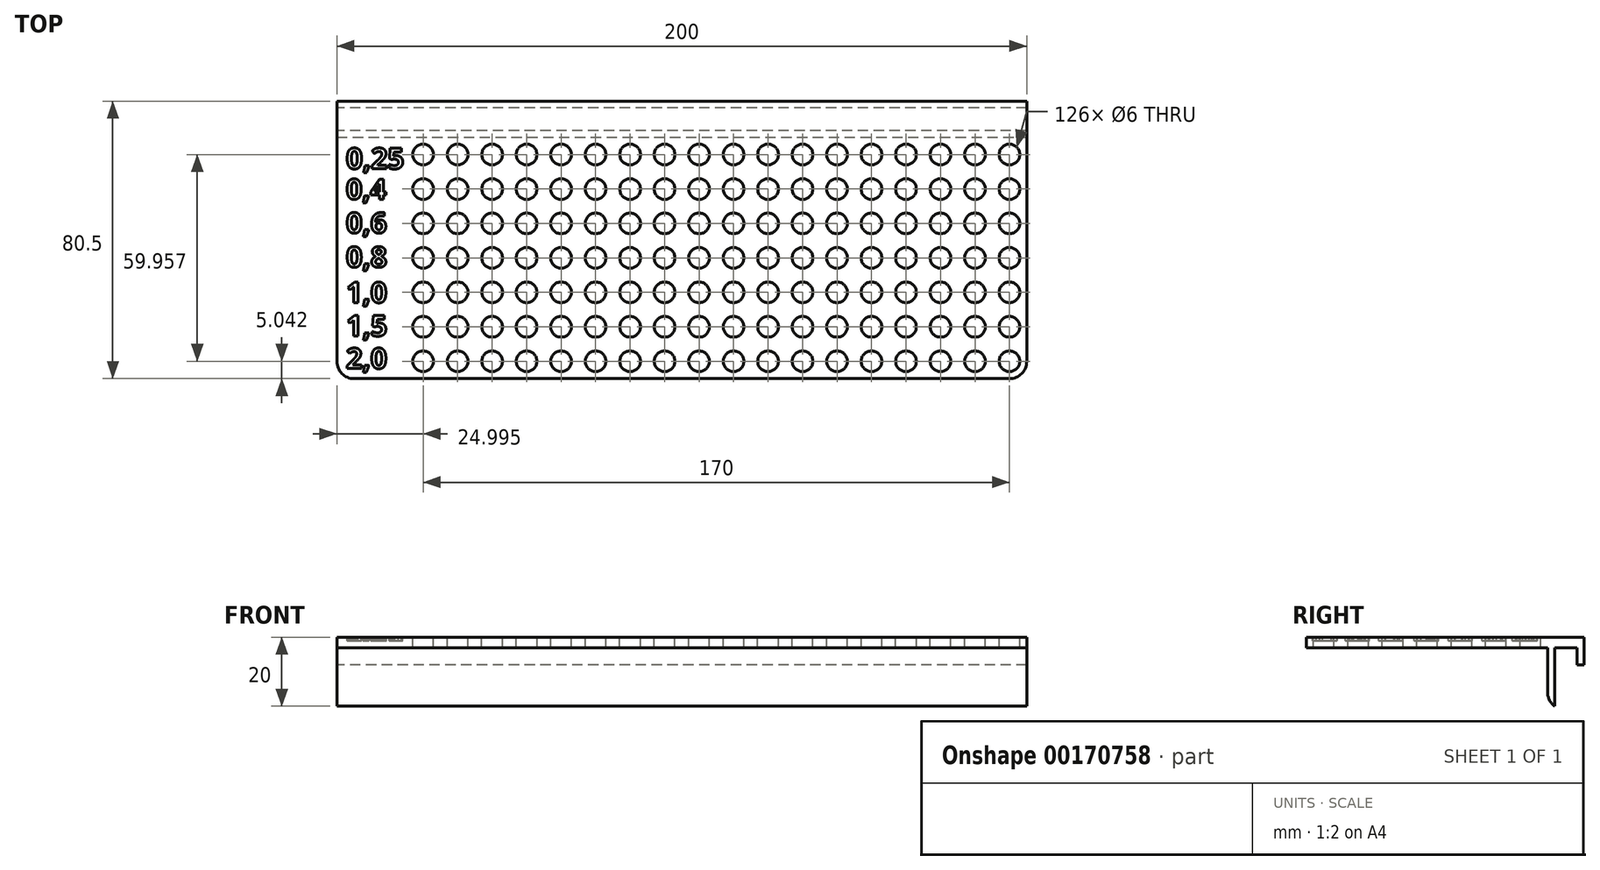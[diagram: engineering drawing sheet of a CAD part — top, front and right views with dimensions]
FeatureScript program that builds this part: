
annotation { "Feature Type Name" : "Feature", "Feature Type Description" : "" }
export const myFeature = defineFeature(function(context is Context, id is Id, definition is map)
    precondition{}
    {
        {
            var Q0;
            Q0=qCreatedBy(makeId("Top.planeOp"),FACE);
            var sketch = newSketch(context, id + "F0", { "sketchPlane" : qUnion([Q0])});
            skLineSegment(sketch, "E0.bottom", {"start": v(-104.06, 75.18) * mm, "end": v(95.94, 75.18) * mm});
            skLineSegment(sketch, "E0.top", {"start": v(-104.06, 5.18) * mm, "end": v(95.94, 5.18) * mm});
            skLineSegment(sketch, "E0.left", {"start": v(-104.06, 75.18) * mm, "end": v(-104.06, 5.18) * mm});
            skLineSegment(sketch, "E0.right", {"start": v(95.94, 75.18) * mm, "end": v(95.94, 5.18) * mm});
            skSolve(sketch);
        }
        {
            var Q0;
            Q0 = qSketchRegion(id + "F0", true);
            extrude(context, id + "F1", {"entities" : qUnion([Q0]), "depth" : 3 * mm});
        }
        {
            var Q0;
            Q0=makeQuery(id+"F1.opExtrude","CAP_FACE",FACE,{"disambiguationData":[OSD([sQuery(id+"F0.wireOp",EDGE,"E0.bottom"),sQuery(id+"F0.wireOp",EDGE,"E0.top"),sQuery(id+"F0.wireOp",EDGE,"E0.left"),sQuery(id+"F0.wireOp",EDGE,"E0.right")])],"isStart":false});
            var sketch = newSketch(context, id + "F2", { "sketchPlane" : qUnion([Q0])});
            skPoint(sketch, "E1", {"position": v(-89.06, 60.18) * mm});
            skPoint(sketch, "E2", {"position": v(-89.06, 50.22) * mm});
            skPoint(sketch, "E3", {"position": v(-89.06, 40.22) * mm});
            skPoint(sketch, "E4", {"position": v(-89.06, 30.22) * mm});
            skPoint(sketch, "E5", {"position": v(-89.06, 70.18) * mm});
            skPoint(sketch, "E6", {"position": v(-79.06, 70.18) * mm});
            skPoint(sketch, "E7", {"position": v(-79.06, 60.18) * mm});
            skPoint(sketch, "E8", {"position": v(-79.06, 50.22) * mm});
            skPoint(sketch, "E9", {"position": v(-79.06, 40.22) * mm});
            skPoint(sketch, "E10", {"position": v(-79.06, 30.22) * mm});
            skPoint(sketch, "E11", {"position": v(-69.06, 70.18) * mm});
            skPoint(sketch, "E12", {"position": v(-69.06, 60.18) * mm});
            skPoint(sketch, "E13", {"position": v(-69.06, 50.22) * mm});
            skPoint(sketch, "E14", {"position": v(-69.06, 40.22) * mm});
            skPoint(sketch, "E15", {"position": v(-69.06, 30.22) * mm});
            skPoint(sketch, "E16", {"position": v(-59.06, 70.18) * mm});
            skPoint(sketch, "E17", {"position": v(-59.06, 60.18) * mm});
            skPoint(sketch, "E18", {"position": v(-59.06, 50.22) * mm});
            skPoint(sketch, "E19", {"position": v(-59.06, 40.22) * mm});
            skPoint(sketch, "E20", {"position": v(-59.06, 30.22) * mm});
            skPoint(sketch, "E21", {"position": v(-49.06, 70.18) * mm});
            skPoint(sketch, "E22", {"position": v(-49.06, 60.18) * mm});
            skPoint(sketch, "E23", {"position": v(-49.06, 50.22) * mm});
            skPoint(sketch, "E24", {"position": v(-49.06, 40.22) * mm});
            skPoint(sketch, "E25", {"position": v(-49.06, 30.22) * mm});
            skPoint(sketch, "E26", {"position": v(-39.06, 70.18) * mm});
            skPoint(sketch, "E27", {"position": v(-39.06, 60.18) * mm});
            skPoint(sketch, "E28", {"position": v(-39.06, 50.22) * mm});
            skPoint(sketch, "E29", {"position": v(-39.06, 40.22) * mm});
            skPoint(sketch, "E30", {"position": v(-39.06, 30.22) * mm});
            skPoint(sketch, "E31", {"position": v(-29.06, 70.18) * mm});
            skPoint(sketch, "E32", {"position": v(-19.06, 70.18) * mm});
            skPoint(sketch, "E33", {"position": v(-9.06, 70.18) * mm});
            skPoint(sketch, "E34", {"position": v(0.94, 70.18) * mm});
            skPoint(sketch, "E35", {"position": v(10.94, 70.18) * mm});
            skPoint(sketch, "E36", {"position": v(20.94, 70.18) * mm});
            skPoint(sketch, "E37", {"position": v(30.94, 70.18) * mm});
            skPoint(sketch, "E38", {"position": v(40.94, 70.18) * mm});
            skPoint(sketch, "E39", {"position": v(50.94, 70.18) * mm});
            skPoint(sketch, "E40", {"position": v(60.94, 70.18) * mm});
            skPoint(sketch, "E41", {"position": v(70.94, 70.18) * mm});
            skPoint(sketch, "E42", {"position": v(80.94, 70.18) * mm});
            skPoint(sketch, "E43", {"position": v(-29.06, 60.18) * mm});
            skPoint(sketch, "E44", {"position": v(-29.06, 50.22) * mm});
            skPoint(sketch, "E45", {"position": v(-29.06, 40.22) * mm});
            skPoint(sketch, "E46", {"position": v(-29.06, 30.22) * mm});
            skPoint(sketch, "E47", {"position": v(90.94, 70.18) * mm});
            skPoint(sketch, "E48", {"position": v(-19.06, 60.18) * mm});
            skPoint(sketch, "E49", {"position": v(-19.06, 50.22) * mm});
            skPoint(sketch, "E50", {"position": v(-19.06, 40.22) * mm});
            skPoint(sketch, "E51", {"position": v(-19.06, 30.22) * mm});
            skPoint(sketch, "E52", {"position": v(-9.06, 60.18) * mm});
            skPoint(sketch, "E53", {"position": v(-9.06, 50.22) * mm});
            skPoint(sketch, "E54", {"position": v(-9.06, 40.22) * mm});
            skPoint(sketch, "E55", {"position": v(-9.06, 30.22) * mm});
            skPoint(sketch, "E56", {"position": v(0.94, 60.18) * mm});
            skPoint(sketch, "E57", {"position": v(0.94, 50.22) * mm});
            skPoint(sketch, "E58", {"position": v(0.94, 40.22) * mm});
            skPoint(sketch, "E59", {"position": v(0.94, 30.22) * mm});
            skPoint(sketch, "E60", {"position": v(10.94, 60.18) * mm});
            skPoint(sketch, "E61", {"position": v(10.94, 50.22) * mm});
            skPoint(sketch, "E62", {"position": v(10.94, 40.22) * mm});
            skPoint(sketch, "E63", {"position": v(10.94, 30.22) * mm});
            skPoint(sketch, "E64", {"position": v(20.94, 60.18) * mm});
            skPoint(sketch, "E65", {"position": v(20.94, 50.22) * mm});
            skPoint(sketch, "E66", {"position": v(20.94, 40.22) * mm});
            skPoint(sketch, "E67", {"position": v(20.94, 30.22) * mm});
            skPoint(sketch, "E68", {"position": v(30.94, 60.18) * mm});
            skPoint(sketch, "E69", {"position": v(30.94, 50.22) * mm});
            skPoint(sketch, "E70", {"position": v(30.94, 40.22) * mm});
            skPoint(sketch, "E71", {"position": v(30.94, 30.22) * mm});
            skPoint(sketch, "E72", {"position": v(40.94, 60.18) * mm});
            skPoint(sketch, "E73", {"position": v(40.94, 50.22) * mm});
            skPoint(sketch, "E74", {"position": v(40.94, 40.22) * mm});
            skPoint(sketch, "E75", {"position": v(40.94, 30.22) * mm});
            skPoint(sketch, "E76", {"position": v(50.94, 60.18) * mm});
            skPoint(sketch, "E77", {"position": v(50.94, 50.22) * mm});
            skPoint(sketch, "E78", {"position": v(50.94, 40.22) * mm});
            skPoint(sketch, "E79", {"position": v(50.94, 30.22) * mm});
            skPoint(sketch, "E80", {"position": v(60.94, 60.18) * mm});
            skPoint(sketch, "E81", {"position": v(60.94, 50.22) * mm});
            skPoint(sketch, "E82", {"position": v(60.94, 40.22) * mm});
            skPoint(sketch, "E83", {"position": v(60.94, 30.22) * mm});
            skPoint(sketch, "E84", {"position": v(70.94, 60.18) * mm});
            skPoint(sketch, "E85", {"position": v(70.94, 50.22) * mm});
            skPoint(sketch, "E86", {"position": v(70.94, 40.22) * mm});
            skPoint(sketch, "E87", {"position": v(70.94, 30.22) * mm});
            skPoint(sketch, "E88", {"position": v(80.94, 60.18) * mm});
            skPoint(sketch, "E89", {"position": v(80.94, 50.22) * mm});
            skPoint(sketch, "E90", {"position": v(80.94, 40.22) * mm});
            skPoint(sketch, "E91", {"position": v(80.94, 30.22) * mm});
            skPoint(sketch, "E92", {"position": v(90.94, 60.18) * mm});
            skPoint(sketch, "E93", {"position": v(90.94, 50.22) * mm});
            skPoint(sketch, "E94", {"position": v(90.94, 40.22) * mm});
            skPoint(sketch, "E95", {"position": v(90.94, 30.22) * mm});
            skPoint(sketch, "E96", {"position": v(-89.06, 20.22) * mm});
            skPoint(sketch, "E97", {"position": v(-89.06, 10.22) * mm});
            skPoint(sketch, "E98", {"position": v(-79.06, 20.22) * mm});
            skPoint(sketch, "E99", {"position": v(-79.06, 10.22) * mm});
            skPoint(sketch, "E100", {"position": v(-69.06, 20.22) * mm});
            skPoint(sketch, "E101", {"position": v(-69.06, 10.22) * mm});
            skPoint(sketch, "E102", {"position": v(-59.06, 20.22) * mm});
            skPoint(sketch, "E103", {"position": v(-59.06, 10.22) * mm});
            skPoint(sketch, "E104", {"position": v(-49.06, 20.22) * mm});
            skPoint(sketch, "E105", {"position": v(-49.06, 10.22) * mm});
            skPoint(sketch, "E106", {"position": v(-39.06, 20.22) * mm});
            skPoint(sketch, "E107", {"position": v(-39.06, 10.22) * mm});
            skPoint(sketch, "E108", {"position": v(-29.06, 20.22) * mm});
            skPoint(sketch, "E109", {"position": v(-29.06, 10.22) * mm});
            skPoint(sketch, "E110", {"position": v(-19.06, 20.22) * mm});
            skPoint(sketch, "E111", {"position": v(-19.06, 10.22) * mm});
            skPoint(sketch, "E112", {"position": v(-9.06, 20.22) * mm});
            skPoint(sketch, "E113", {"position": v(-9.06, 10.22) * mm});
            skPoint(sketch, "E114", {"position": v(0.94, 20.22) * mm});
            skPoint(sketch, "E115", {"position": v(0.94, 10.22) * mm});
            skPoint(sketch, "E116", {"position": v(10.94, 20.22) * mm});
            skPoint(sketch, "E117", {"position": v(10.94, 10.22) * mm});
            skPoint(sketch, "E118", {"position": v(20.94, 20.22) * mm});
            skPoint(sketch, "E119", {"position": v(20.94, 10.22) * mm});
            skPoint(sketch, "E120", {"position": v(30.94, 20.22) * mm});
            skPoint(sketch, "E121", {"position": v(30.94, 10.22) * mm});
            skPoint(sketch, "E122", {"position": v(40.94, 20.22) * mm});
            skPoint(sketch, "E123", {"position": v(40.94, 10.22) * mm});
            skPoint(sketch, "E124", {"position": v(50.94, 20.22) * mm});
            skPoint(sketch, "E125", {"position": v(50.94, 10.22) * mm});
            skPoint(sketch, "E126", {"position": v(60.94, 20.22) * mm});
            skPoint(sketch, "E127", {"position": v(60.94, 10.22) * mm});
            skPoint(sketch, "E128", {"position": v(70.94, 20.22) * mm});
            skPoint(sketch, "E129", {"position": v(70.94, 10.22) * mm});
            skPoint(sketch, "E130", {"position": v(80.94, 20.22) * mm});
            skPoint(sketch, "E131", {"position": v(80.94, 10.22) * mm});
            skPoint(sketch, "E132", {"position": v(90.94, 20.22) * mm});
            skPoint(sketch, "E133", {"position": v(90.94, 10.22) * mm});
            skSolve(sketch);
        }
        {
            var Q0;
            Q0=sQuery(id+"F2.wireOp",VERTEX,"E26");
            var Q1;
            Q1=sQuery(id+"F2.wireOp",VERTEX,"E105");
            var Q2;
            Q2=sQuery(id+"F2.wireOp",VERTEX,"E13");
            var Q3;
            Q3=sQuery(id+"F2.wireOp",VERTEX,"E12");
            var Q4;
            Q4=sQuery(id+"F2.wireOp",VERTEX,"E57");
            var Q5;
            Q5=sQuery(id+"F2.wireOp",VERTEX,"E8");
            var Q6;
            Q6=sQuery(id+"F2.wireOp",VERTEX,"E10");
            var Q7;
            Q7=sQuery(id+"F2.wireOp",VERTEX,"E9");
            var Q8;
            Q8=sQuery(id+"F2.wireOp",VERTEX,"E113");
            var Q9;
            Q9=sQuery(id+"F2.wireOp",VERTEX,"E101");
            var Q10;
            Q10=sQuery(id+"F2.wireOp",VERTEX,"E100");
            var Q11;
            Q11=sQuery(id+"F2.wireOp",VERTEX,"E18");
            var Q12;
            Q12=sQuery(id+"F2.wireOp",VERTEX,"E109");
            var Q13;
            Q13=sQuery(id+"F2.wireOp",VERTEX,"E7");
            var Q14;
            Q14=sQuery(id+"F2.wireOp",VERTEX,"E35");
            var Q15;
            Q15=sQuery(id+"F2.wireOp",VERTEX,"E51");
            var Q16;
            Q16=sQuery(id+"F2.wireOp",VERTEX,"E16");
            var Q17;
            Q17=sQuery(id+"F2.wireOp",VERTEX,"E11");
            var Q18;
            Q18=sQuery(id+"F2.wireOp",VERTEX,"E50");
            var Q19;
            Q19=sQuery(id+"F2.wireOp",VERTEX,"E110");
            var Q20;
            Q20=sQuery(id+"F2.wireOp",VERTEX,"E117");
            var Q21;
            Q21=sQuery(id+"F2.wireOp",VERTEX,"E15");
            var Q22;
            Q22=sQuery(id+"F2.wireOp",VERTEX,"E14");
            var Q23;
            Q23=sQuery(id+"F2.wireOp",VERTEX,"E19");
            var Q24;
            Q24=sQuery(id+"F2.wireOp",VERTEX,"E6");
            var Q25;
            Q25=sQuery(id+"F2.wireOp",VERTEX,"E116");
            var Q26;
            Q26=sQuery(id+"F2.wireOp",VERTEX,"E31");
            var Q27;
            Q27=sQuery(id+"F2.wireOp",VERTEX,"E34");
            var Q28;
            Q28=sQuery(id+"F2.wireOp",VERTEX,"E112");
            var Q29;
            Q29=sQuery(id+"F2.wireOp",VERTEX,"E54");
            var Q30;
            Q30=sQuery(id+"F2.wireOp",VERTEX,"E60");
            var Q31;
            Q31=sQuery(id+"F2.wireOp",VERTEX,"E62");
            var Q32;
            Q32=sQuery(id+"F2.wireOp",VERTEX,"E104");
            var Q33;
            Q33=sQuery(id+"F2.wireOp",VERTEX,"E22");
            var Q34;
            Q34=sQuery(id+"F2.wireOp",VERTEX,"E48");
            var Q35;
            Q35=sQuery(id+"F2.wireOp",VERTEX,"E32");
            var Q36;
            Q36=sQuery(id+"F2.wireOp",VERTEX,"E52");
            var Q37;
            Q37=sQuery(id+"F2.wireOp",VERTEX,"E63");
            var Q38;
            Q38=sQuery(id+"F2.wireOp",VERTEX,"E45");
            var Q39;
            Q39=sQuery(id+"F2.wireOp",VERTEX,"E20");
            var Q40;
            Q40=sQuery(id+"F2.wireOp",VERTEX,"E29");
            var Q41;
            Q41=sQuery(id+"F2.wireOp",VERTEX,"E107");
            var Q42;
            Q42=sQuery(id+"F2.wireOp",VERTEX,"E24");
            var Q43;
            Q43=sQuery(id+"F2.wireOp",VERTEX,"E23");
            var Q44;
            Q44=sQuery(id+"F2.wireOp",VERTEX,"E56");
            var Q45;
            Q45=sQuery(id+"F2.wireOp",VERTEX,"E103");
            var Q46;
            Q46=sQuery(id+"F2.wireOp",VERTEX,"E25");
            var Q47;
            Q47=sQuery(id+"F2.wireOp",VERTEX,"E114");
            var Q48;
            Q48=sQuery(id+"F2.wireOp",VERTEX,"E98");
            var Q49;
            Q49=sQuery(id+"F2.wireOp",VERTEX,"E55");
            var Q50;
            Q50=sQuery(id+"F2.wireOp",VERTEX,"E43");
            var Q51;
            Q51=sQuery(id+"F2.wireOp",VERTEX,"E58");
            var Q52;
            Q52=sQuery(id+"F2.wireOp",VERTEX,"E27");
            var Q53;
            Q53=sQuery(id+"F2.wireOp",VERTEX,"E106");
            var Q54;
            Q54=sQuery(id+"F2.wireOp",VERTEX,"E21");
            var Q55;
            Q55=sQuery(id+"F2.wireOp",VERTEX,"E28");
            var Q56;
            Q56=sQuery(id+"F2.wireOp",VERTEX,"E44");
            var Q57;
            Q57=sQuery(id+"F2.wireOp",VERTEX,"E59");
            var Q58;
            Q58=sQuery(id+"F2.wireOp",VERTEX,"E61");
            var Q59;
            Q59=sQuery(id+"F2.wireOp",VERTEX,"E111");
            var Q60;
            Q60=sQuery(id+"F2.wireOp",VERTEX,"E46");
            var Q61;
            Q61=sQuery(id+"F2.wireOp",VERTEX,"E33");
            var Q62;
            Q62=sQuery(id+"F2.wireOp",VERTEX,"E53");
            var Q63;
            Q63=sQuery(id+"F2.wireOp",VERTEX,"E49");
            var Q64;
            Q64=sQuery(id+"F2.wireOp",VERTEX,"E30");
            var Q65;
            Q65=sQuery(id+"F2.wireOp",VERTEX,"E108");
            var Q66;
            Q66=sQuery(id+"F2.wireOp",VERTEX,"E115");
            var Q67;
            Q67=sQuery(id+"F2.wireOp",VERTEX,"E99");
            var Q68;
            Q68=sQuery(id+"F2.wireOp",VERTEX,"E102");
            var Q69;
            Q69=sQuery(id+"F2.wireOp",VERTEX,"E17");
            var Q70;
            Q70=sQuery(id+"F2.wireOp",VERTEX,"E36");
            var Q71;
            Q71=sQuery(id+"F2.wireOp",VERTEX,"E37");
            var Q72;
            Q72=sQuery(id+"F2.wireOp",VERTEX,"E65");
            var Q73;
            Q73=sQuery(id+"F2.wireOp",VERTEX,"E66");
            var Q74;
            Q74=sQuery(id+"F2.wireOp",VERTEX,"E69");
            var Q75;
            Q75=sQuery(id+"F2.wireOp",VERTEX,"E120");
            var Q76;
            Q76=sQuery(id+"F2.wireOp",VERTEX,"E67");
            var Q77;
            Q77=sQuery(id+"F2.wireOp",VERTEX,"E70");
            var Q78;
            Q78=sQuery(id+"F2.wireOp",VERTEX,"E119");
            var Q79;
            Q79=sQuery(id+"F2.wireOp",VERTEX,"E121");
            var Q80;
            Q80=sQuery(id+"F2.wireOp",VERTEX,"E68");
            var Q81;
            Q81=sQuery(id+"F2.wireOp",VERTEX,"E64");
            var Q82;
            Q82=sQuery(id+"F2.wireOp",VERTEX,"E71");
            var Q83;
            Q83=sQuery(id+"F2.wireOp",VERTEX,"E118");
            var Q84;
            Q84=sQuery(id+"F2.wireOp",VERTEX,"E122");
            var Q85;
            Q85=sQuery(id+"F2.wireOp",VERTEX,"E123");
            var Q86;
            Q86=sQuery(id+"F2.wireOp",VERTEX,"E125");
            var Q87;
            Q87=sQuery(id+"F2.wireOp",VERTEX,"E124");
            var Q88;
            Q88=makeQuery(id+"F1.opExtrude","SWEPT_BODY",BODY,{"disambiguationData":[OSD([sQuery(id+"F0.wireOp",EDGE,"E0.bottom"),sQuery(id+"F0.wireOp",EDGE,"E0.top"),sQuery(id+"F0.wireOp",EDGE,"E0.left"),sQuery(id+"F0.wireOp",EDGE,"E0.right")])]});
            hole(context, id + "F3", {"style" : HoleStyle.SIMPLE, "endStyle" : HoleEndStyle.THROUGH, "holeDiameter" : 6 * mm, "locations" : qUnion([Q0, Q1, Q2, Q3, Q4, Q5, Q6, Q7, Q8, Q9, Q10, Q11, Q12, Q13, Q14, Q15, Q16, Q17, Q18, Q19, Q20, Q21, Q22, Q23, Q24, Q25, Q26, Q27, Q28, Q29, Q30, Q31, Q32, Q33, Q34, Q35, Q36, Q37, Q38, Q39, Q40, Q41, Q42, Q43, Q44, Q45, Q46, Q47, Q48, Q49, Q50, Q51, Q52, Q53, Q54, Q55, Q56, Q57, Q58, Q59, Q60, Q61, Q62, Q63, Q64, Q65, Q66, Q67, Q68, Q69, Q70, Q71, Q72, Q73, Q74, Q75, Q76, Q77, Q78, Q79, Q80, Q81, Q82, Q83, Q84, Q85, Q86, Q87]), "scope" : qUnion([Q88]), "isTappedThrough" : true});
        }
        {
            var Q0;
            Q0=sQuery(id+"F2.wireOp",VERTEX,"E39");
            var Q1;
            Q1=sQuery(id+"F2.wireOp",VERTEX,"E38");
            var Q2;
            Q2=sQuery(id+"F2.wireOp",VERTEX,"E77");
            var Q3;
            Q3=sQuery(id+"F2.wireOp",VERTEX,"E73");
            var Q4;
            Q4=sQuery(id+"F2.wireOp",VERTEX,"E78");
            var Q5;
            Q5=sQuery(id+"F2.wireOp",VERTEX,"E72");
            var Q6;
            Q6=sQuery(id+"F2.wireOp",VERTEX,"E75");
            var Q7;
            Q7=sQuery(id+"F2.wireOp",VERTEX,"E74");
            var Q8;
            Q8=sQuery(id+"F2.wireOp",VERTEX,"E76");
            var Q9;
            Q9=sQuery(id+"F2.wireOp",VERTEX,"E79");
            var Q10;
            Q10=sQuery(id+"F2.wireOp",VERTEX,"E128");
            var Q11;
            Q11=sQuery(id+"F2.wireOp",VERTEX,"E81");
            var Q12;
            Q12=sQuery(id+"F2.wireOp",VERTEX,"E80");
            var Q13;
            Q13=sQuery(id+"F2.wireOp",VERTEX,"E127");
            var Q14;
            Q14=sQuery(id+"F2.wireOp",VERTEX,"E84");
            var Q15;
            Q15=sQuery(id+"F2.wireOp",VERTEX,"E82");
            var Q16;
            Q16=sQuery(id+"F2.wireOp",VERTEX,"E85");
            var Q17;
            Q17=sQuery(id+"F2.wireOp",VERTEX,"E87");
            var Q18;
            Q18=sQuery(id+"F2.wireOp",VERTEX,"E129");
            var Q19;
            Q19=sQuery(id+"F2.wireOp",VERTEX,"E41");
            var Q20;
            Q20=sQuery(id+"F2.wireOp",VERTEX,"E40");
            var Q21;
            Q21=sQuery(id+"F2.wireOp",VERTEX,"E83");
            var Q22;
            Q22=sQuery(id+"F2.wireOp",VERTEX,"E126");
            var Q23;
            Q23=sQuery(id+"F2.wireOp",VERTEX,"E86");
            var Q24;
            Q24=sQuery(id+"F2.wireOp",VERTEX,"E94");
            var Q25;
            Q25=sQuery(id+"F2.wireOp",VERTEX,"E131");
            var Q26;
            Q26=sQuery(id+"F2.wireOp",VERTEX,"E93");
            var Q27;
            Q27=sQuery(id+"F2.wireOp",VERTEX,"E42");
            var Q28;
            Q28=sQuery(id+"F2.wireOp",VERTEX,"E132");
            var Q29;
            Q29=sQuery(id+"F2.wireOp",VERTEX,"E47");
            var Q30;
            Q30=sQuery(id+"F2.wireOp",VERTEX,"E88");
            var Q31;
            Q31=sQuery(id+"F2.wireOp",VERTEX,"E91");
            var Q32;
            Q32=sQuery(id+"F2.wireOp",VERTEX,"E90");
            var Q33;
            Q33=sQuery(id+"F2.wireOp",VERTEX,"E89");
            var Q34;
            Q34=sQuery(id+"F2.wireOp",VERTEX,"E95");
            var Q35;
            Q35=sQuery(id+"F2.wireOp",VERTEX,"E130");
            var Q36;
            Q36=sQuery(id+"F2.wireOp",VERTEX,"E133");
            var Q37;
            Q37=sQuery(id+"F2.wireOp",VERTEX,"E92");
            var Q38;
            Q38=makeQuery(id+"F1.opExtrude","SWEPT_BODY",BODY,{"disambiguationData":[OSD([sQuery(id+"F0.wireOp",EDGE,"E0.bottom"),sQuery(id+"F0.wireOp",EDGE,"E0.top"),sQuery(id+"F0.wireOp",EDGE,"E0.left"),sQuery(id+"F0.wireOp",EDGE,"E0.right")])]});
            hole(context, id + "F4", {"style" : HoleStyle.SIMPLE, "endStyle" : HoleEndStyle.THROUGH, "holeDiameter" : 6 * mm, "locations" : qUnion([Q0, Q1, Q2, Q3, Q4, Q5, Q6, Q7, Q8, Q9, Q10, Q11, Q12, Q13, Q14, Q15, Q16, Q17, Q18, Q19, Q20, Q21, Q22, Q23, Q24, Q25, Q26, Q27, Q28, Q29, Q30, Q31, Q32, Q33, Q34, Q35, Q36, Q37]), "scope" : qUnion([Q38]), "isTappedThrough" : true});
        }
        {
            var Q0;
            Q0=makeQuery(id+"F2.imprint","IMPRINT",FACE,{"disambiguationData":[TD([[makeQuery(id+"F2.imprint","IMPRINT",EDGE,{"derivedFrom":makeQuery(id+"F1.opExtrude","CAP_EDGE",EDGE,{"disambiguationData":[OSD([sQuery(id+"F0.wireOp",EDGE,"E0.bottom")])],"isStart":false})}),-1.0]])]});
            var sketch = newSketch(context, id + "F5", { "sketchPlane" : qUnion([Q0])});
            skText(sketch, "E134", { "text": "0,25", "fontName": "OpenSans-Bold.ttf"});
            skText(sketch, "E135", { "text": "0,4", "fontName": "OpenSans-Bold.ttf"});
            skPoint(sketch, "E135.firstSnap0", {"position": v(-101.4, 69.06) * mm});
            skText(sketch, "E136", { "text": "0,6", "fontName": "OpenSans-Bold.ttf"});
            skText(sketch, "E137", { "text": "0,8", "fontName": "OpenSans-Bold.ttf"});
            skText(sketch, "E138", { "text": "1,0", "fontName": "OpenSans-Bold.ttf"});
            skText(sketch, "E139", { "text": "1,5", "fontName": "OpenSans-Bold.ttf"});
            skText(sketch, "E140", { "text": "2,0\n", "fontName": "OpenSans-Bold.ttf"});
            const initialGuessF5  = {"E134": [-0.1014, 0.06604, 1, 0, 0.00604], "E135": [-0.1014, 0.05723, 1, 0, 0.00587], "E136": [-0.1014, 0.04743, 1, 0, 0.00593], "E137": [-0.1014, 0.03752, 1, 0, 0.00595], "E138": [-0.1014, 0.02722, 1, 0, 0.00595], "E139": [-0.1014, 0.01754, 1, 0, 0.00599], "E140": [-0.1014, 0.00811, 1, 0, 0.00595]};
            skSetInitialGuess(sketch, initialGuessF5);
            skSolve(sketch);
        }
        {
            var Q0;
            Q0 = qSketchRegion(id + "F5", true);
            extrude(context, id + "F6", {"entities" : qUnion([Q0]), "operationType" : NewBodyOperationType.REMOVE, "oppositeDirection" : true, "depth" : 1 * mm});
        }
        {
            var Q0;
            Q0=makeQuery(id+"F1.opExtrude","SWEPT_FACE",FACE,{"disambiguationData":[OSD([sQuery(id+"F0.wireOp",EDGE,"E0.bottom")])]});
            var sketch = newSketch(context, id + "F7", { "sketchPlane" : qUnion([Q0])});
            skPoint(sketch, "E141.oppositeSnap0", {"position": v(104.06, 1.5) * mm});
            skLineSegment(sketch, "E141.bottom", {"start": v(-95.94, 3) * mm, "end": v(104.06, 3) * mm});
            skLineSegment(sketch, "E141.top", {"start": v(-95.94, -17) * mm, "end": v(104.06, -17) * mm});
            skLineSegment(sketch, "E141.left", {"start": v(-95.94, 3) * mm, "end": v(-95.94, -17) * mm});
            skLineSegment(sketch, "E141.right", {"start": v(104.06, 3) * mm, "end": v(104.06, -17) * mm});
            skSolve(sketch);
        }
        {
            var Q0;
            Q0 = qSketchRegion(id + "F7", true);
            extrude(context, id + "F8", {"entities" : qUnion([Q0]), "operationType" : NewBodyOperationType.ADD, "depth" : 2 * mm});
        }
        {
            var Q0;
            Q0=makeQuery(id+"F8.opExtrude","CAP_FACE",FACE,{"disambiguationData":[OSD([sQuery(id+"F7.wireOp",EDGE,"E141.bottom"),sQuery(id+"F7.wireOp",EDGE,"E141.top"),sQuery(id+"F7.wireOp",EDGE,"E141.left"),sQuery(id+"F7.wireOp",EDGE,"E141.right")])],"isStart":false});
            var sketch = newSketch(context, id + "F9", { "sketchPlane" : qUnion([Q0])});
            skLineSegment(sketch, "E142.bottom", {"start": v(-95.94, 3) * mm, "end": v(104.06, 3) * mm});
            skLineSegment(sketch, "E142.top", {"start": v(-95.94, 0) * mm, "end": v(104.06, 0) * mm});
            skLineSegment(sketch, "E142.left", {"start": v(-95.94, 3) * mm, "end": v(-95.94, 0) * mm});
            skLineSegment(sketch, "E142.right", {"start": v(104.06, 3) * mm, "end": v(104.06, 0) * mm});
            skSolve(sketch);
        }
        {
            var Q0;
            Q0 = qSketchRegion(id + "F9", true);
            extrude(context, id + "F10", {"entities" : qUnion([Q0]), "operationType" : NewBodyOperationType.ADD, "depth" : 6.5 * mm});
        }
        {
            var Q0;
            Q0=makeQuery(id+"F10.opExtrude","CAP_FACE",FACE,{"disambiguationData":[OSD([sQuery(id+"F9.wireOp",EDGE,"E142.bottom"),sQuery(id+"F9.wireOp",EDGE,"E142.top"),sQuery(id+"F9.wireOp",EDGE,"E142.left"),sQuery(id+"F9.wireOp",EDGE,"E142.right")])],"isStart":false});
            var sketch = newSketch(context, id + "F11", { "sketchPlane" : qUnion([Q0])});
            skLineSegment(sketch, "E143.bottom", {"start": v(-95.94, 3) * mm, "end": v(104.06, 3) * mm});
            skLineSegment(sketch, "E143.top", {"start": v(-95.94, -5) * mm, "end": v(104.06, -5) * mm});
            skLineSegment(sketch, "E143.left", {"start": v(-95.94, 3) * mm, "end": v(-95.94, -5) * mm});
            skLineSegment(sketch, "E143.right", {"start": v(104.06, 3) * mm, "end": v(104.06, -5) * mm});
            skSolve(sketch);
        }
        {
            var Q0;
            Q0 = qSketchRegion(id + "F11", true);
            extrude(context, id + "F12", {"entities" : qUnion([Q0]), "operationType" : NewBodyOperationType.ADD, "depth" : 2 * mm});
        }
        {
            var Q0;
            Q0=makeQuery(id+"F1.opExtrude","SWEPT_EDGE",EDGE,{"disambiguationData":[OSD([sQuery(id+"F0.wireOp",EDGE,"E0.top"),sQuery(id+"F0.wireOp",EDGE,"E0.left")])]});
            var Q1;
            Q1=makeQuery(id+"F1.opExtrude","SWEPT_EDGE",EDGE,{"disambiguationData":[OSD([sQuery(id+"F0.wireOp",EDGE,"E0.top"),sQuery(id+"F0.wireOp",EDGE,"E0.right")])]});
            var Q2;
            Q2=makeQuery(id+"F8.opExtrude","CAP_EDGE",EDGE,{"disambiguationData":[OSD([sQuery(id+"F7.wireOp",EDGE,"E141.top")])],"isStart":true});
            fillet(context, id + "F13", {"entities" : qUnion([Q0, Q1, Q2]), "radius" : 5 * mm, "tangentPropagation" : true, "allowEdgeOverflow" : false});
        }
    });
